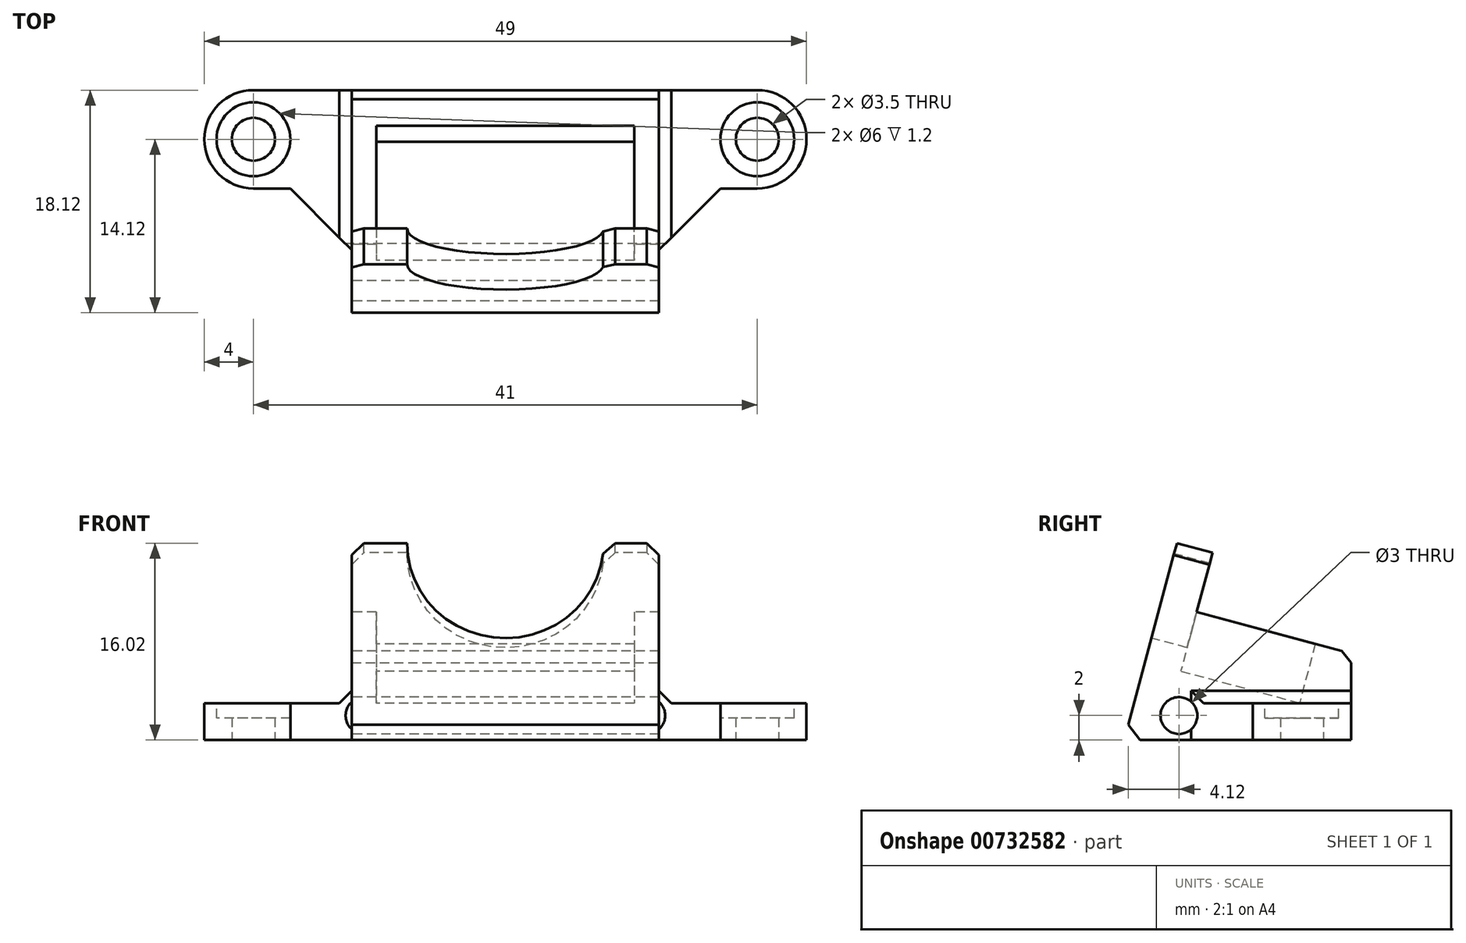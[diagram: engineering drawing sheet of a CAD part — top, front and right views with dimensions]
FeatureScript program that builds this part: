
annotation { "Feature Type Name" : "Feature", "Feature Type Description" : "" }
export const myFeature = defineFeature(function(context is Context, id is Id, definition is map)
    precondition{}
    {
        {
            var Q0;
            Q0=qCreatedBy(makeId("Top.planeOp"),FACE);
            var sketch = newSketch(context, id + "F0", { "sketchPlane" : qUnion([Q0])});
            skLineSegment(sketch, "E0.bottom", {"start": v(20.5, 4) * mm, "end": v(-20.5, 4) * mm});
            skLineSegment(sketch, "E0.top", {"start": v(20.5, -4) * mm, "end": v(-20.5, -4) * mm});
            skLineSegment(sketch, "E0.left", {"start": v(20.5, 4) * mm, "end": v(20.5, -4) * mm});
            skLineSegment(sketch, "E0.right", {"start": v(-20.5, 4) * mm, "end": v(-20.5, -4) * mm});
            skPoint(sketch, "E0.middle", {"position": v(0, 0) * mm});
            skCircle(sketch, "E1", {"center": v(20.5, 0) * mm, "radius": 4 * mm});
            skCircle(sketch, "E2", {"center": v(-20.5, 0) * mm, "radius": 4 * mm});
            skCircle(sketch, "E3", {"center": v(-20.5, 0) * mm, "radius": 1.75 * mm});
            skCircle(sketch, "E4", {"center": v(20.5, 0) * mm, "radius": 1.75 * mm});
            skSolve(sketch);
        }
        {
            var Q0;
            Q0=qCreatedBy(makeId("Right.planeOp"),FACE);
            var sketch = newSketch(context, id + "F1", { "sketchPlane" : qUnion([Q0])});
            skLineSegment(sketch, "E5", {"start": v(0, 0) * mm, "end": v(-14.45, 0) * mm});
            skLineSegment(sketch, "E6", {"start": v(-14.45, 0) * mm, "end": v(-10.16, 16.02) * mm});
            skLineSegment(sketch, "E7", {"start": v(-10.16, 16.02) * mm, "end": v(-7.26, 15.25) * mm});
            skLineSegment(sketch, "E8", {"start": v(-7.26, 15.25) * mm, "end": v(-9.85, 5.59) * mm});
            skLineSegment(sketch, "E9", {"start": v(-9.85, 5.59) * mm, "end": v(-0.2, 3) * mm});
            skLineSegment(sketch, "E10", {"start": v(-0.2, 3) * mm, "end": v(1.1, 7.83) * mm});
            skLineSegment(sketch, "E11", {"start": v(1.1, 7.83) * mm, "end": v(4, 7.05) * mm});
            skLineSegment(sketch, "E12", {"start": v(4, 0) * mm, "end": v(0, 0) * mm});
            skLineSegment(sketch, "E13", {"start": v(4, 7.05) * mm, "end": v(4, 0) * mm});
            skSolve(sketch);
        }
        {
            var Q0;
            Q0 = qSketchRegion(id + "F0", true);
            extrude(context, id + "F2", {"entities" : qUnion([Q0]), "depth" : 3 * mm, "offsetDistance" : 25 * mm});
        }
        {
            var Q0;
            Q0=makeQuery(id+"F2.opExtrude","CAP_FACE",FACE,{"disambiguationData":[OSD([sQuery(id+"F0.wireOp",EDGE,"E0.bottom"),sQuery(id+"F0.wireOp",EDGE,"E0.top"),sQuery(id+"F0.wireOp",EDGE,"E1"),sQuery(id+"F0.wireOp",EDGE,"E2"),sQuery(id+"F0.wireOp",EDGE,"E3"),sQuery(id+"F0.wireOp",EDGE,"E4")])],"isStart":false});
            var sketch = newSketch(context, id + "F3", { "sketchPlane" : qUnion([Q0])});
            skCircle(sketch, "E14", {"center": v(-20.5, 0) * mm, "radius": 3 * mm});
            skCircle(sketch, "E15", {"center": v(20.5, 0) * mm, "radius": 3 * mm});
            skSolve(sketch);
        }
        {
            var Q0;
            Q0 = qSketchRegion(id + "F3", true);
            extrude(context, id + "F4", {"entities" : qUnion([Q0]), "operationType" : NewBodyOperationType.REMOVE, "oppositeDirection" : true, "depth" : 1.2 * mm, "offsetDistance" : 25 * mm});
        }
        {
            var Q0;
            Q0 = qSketchRegion(id + "F1", true);
            extrude(context, id + "F5", {"entities" : qUnion([Q0]), "operationType" : NewBodyOperationType.ADD, "endBound" : BoundingType.SYMMETRIC, "depth" : 25 * mm, "offsetDistance" : 25 * mm});
        }
        {
            var Q0;
            Q0=makeQuery(id+"F5.opExtrude","SWEPT_FACE",FACE,{"disambiguationData":[OSD([sQuery(id+"F1.wireOp",EDGE,"E9")])]});
            var sketch = newSketch(context, id + "F6", { "sketchPlane" : qUnion([Q0])});
            skLineSegment(sketch, "E16", {"start": v(10.5, -10.96) * mm, "end": v(10.5, -0.96) * mm});
            skLineSegment(sketch, "E17", {"start": v(10.5, -0.96) * mm, "end": v(-10.5, -0.96) * mm, "construction": true});
            skLineSegment(sketch, "E18", {"start": v(-10.5, -0.96) * mm, "end": v(-10.5, -10.96) * mm});
            skLineSegment(sketch, "E19", {"start": v(-10.5, -10.96) * mm, "end": v(10.5, -10.96) * mm, "construction": true});
            skPoint(sketch, "E20", {"position": v(0, -0.96) * mm});
            skLineSegment(sketch, "E21", {"start": v(0, 0) * mm, "end": v(0, -0.96) * mm, "construction": true});
            skLineSegment(sketch, "E22.0", {"start": v(12.5, -10.96) * mm, "end": v(12.5, -0.96) * mm});
            skLineSegment(sketch, "E23.0", {"start": v(-12.5, -10.96) * mm, "end": v(-12.5, -0.96) * mm});
            skLineSegment(sketch, "E24", {"start": v(-10.5, -10.96) * mm, "end": v(-12.5, -10.96) * mm});
            skLineSegment(sketch, "E25", {"start": v(-10.5, -0.96) * mm, "end": v(-12.5, -0.96) * mm});
            skLineSegment(sketch, "E26", {"start": v(10.5, -0.96) * mm, "end": v(12.5, -0.96) * mm});
            skLineSegment(sketch, "E27", {"start": v(12.5, -10.96) * mm, "end": v(10.5, -10.96) * mm});
            skSolve(sketch);
        }
        {
            var Q0;
            Q0 = qSketchRegion(id + "F6", true);
            var Q1;
            Q1=makeQuery(id+"F5.opExtrude","SWEPT_FACE",FACE,{"disambiguationData":[OSD([sQuery(id+"F1.wireOp",EDGE,"E11")])]});
            extrude(context, id + "F7", {"entities" : qUnion([Q0]), "operationType" : NewBodyOperationType.ADD, "endBound" : BoundingType.UP_TO_SURFACE, "depth" : 25 * mm, "endBoundEntityFace" : qUnion([Q1]), "offsetDistance" : 25 * mm});
        }
        {
            var Q0;
            Q0=makeQuery(id+"F5.opExtrude","SWEPT_FACE",FACE,{"disambiguationData":[OSD([sQuery(id+"F1.wireOp",EDGE,"E6")])]});
            var sketch = newSketch(context, id + "F8", { "sketchPlane" : qUnion([Q0])});
            skCircle(sketch, "E28", {"center": v(0, 12.85) * mm, "radius": 8 * mm});
            skSolve(sketch);
        }
        {
            var Q0;
            {var subQ0=sQuery(id+"F8.wireOp",EDGE,"E28");var subQ1=makeQuery(id+"F5.opExtrude","SWEPT_EDGE",EDGE,{"disambiguationData":[OSD([sQuery(id+"F1.wireOp",EDGE,"E6"),sQuery(id+"F1.wireOp",EDGE,"E7")])]});var subQ2=makeQuery(id+"F8.imprint","INTERSECT",VERTEX,{"disambiguationData":[OD(0.0)],"derivedFrom":[subQ1,subQ0]});Q0=makeQuery(id+"F8.imprint","IMPRINT",FACE,{"disambiguationData":[TD([[makeQuery(id+"F8.imprint","IMPRINT",EDGE,{"disambiguationData":[TD([[subQ2,-1.0]])],"derivedFrom":subQ0}),1.0]])]});}
            extrude(context, id + "F9", {"entities" : qUnion([Q0]), "operationType" : NewBodyOperationType.REMOVE, "endBound" : BoundingType.UP_TO_NEXT, "oppositeDirection" : true, "depth" : 25 * mm, "offsetDistance" : 25 * mm});
        }
        {
            var Q0;
            Q0=makeQuery(id+"F5.boolean.opBoolean","INTERSECT",EDGE,{"derivedFrom":[makeQuery(id+"F2.opExtrude","SWEPT_FACE",FACE,{"disambiguationData":[OSD([sQuery(id+"F0.wireOp",EDGE,"E0.top")])]}),makeQuery(id+"F5.opExtrude","CAP_FACE",FACE,{"disambiguationData":[OSD([sQuery(id+"F1.wireOp",EDGE,"E5"),sQuery(id+"F1.wireOp",EDGE,"E6"),sQuery(id+"F1.wireOp",EDGE,"E7"),sQuery(id+"F1.wireOp",EDGE,"E8"),sQuery(id+"F1.wireOp",EDGE,"E9"),sQuery(id+"F1.wireOp",EDGE,"E10"),sQuery(id+"F1.wireOp",EDGE,"E11"),sQuery(id+"F1.wireOp",EDGE,"E12"),sQuery(id+"F1.wireOp",EDGE,"E13")])],"isStart":true})]});
            var Q1;
            Q1=makeQuery(id+"F5.boolean.opBoolean","INTERSECT",EDGE,{"derivedFrom":[makeQuery(id+"F2.opExtrude","SWEPT_FACE",FACE,{"disambiguationData":[OSD([sQuery(id+"F0.wireOp",EDGE,"E0.top")])]}),makeQuery(id+"F5.opExtrude","CAP_FACE",FACE,{"disambiguationData":[OSD([sQuery(id+"F1.wireOp",EDGE,"E5"),sQuery(id+"F1.wireOp",EDGE,"E6"),sQuery(id+"F1.wireOp",EDGE,"E7"),sQuery(id+"F1.wireOp",EDGE,"E8"),sQuery(id+"F1.wireOp",EDGE,"E9"),sQuery(id+"F1.wireOp",EDGE,"E10"),sQuery(id+"F1.wireOp",EDGE,"E11"),sQuery(id+"F1.wireOp",EDGE,"E12"),sQuery(id+"F1.wireOp",EDGE,"E13")])],"isStart":false})]});
            chamfer(context, id + "F10", {"entities" : qUnion([Q0, Q1]), "width" : 5 * mm, "tangentPropagation" : true});
        }
        {
            var Q0;
            {var subQ0=sQuery(id+"F8.wireOp",EDGE,"E28");var subQ1=sQuery(id+"F1.wireOp",EDGE,"E7");var subQ2=sQuery(id+"F1.wireOp",EDGE,"E6");Q0=makeQuery(id+"F9.boolean.opBoolean","COPY",EDGE,{"derivedFrom":makeQuery(id+"F9.opExtrude","SWEPT_EDGE",EDGE,{"disambiguationData":[OSD([subQ2,subQ1,subQ0]),TDD([makeQuery(id+"F8.imprint","INTERSECT",VERTEX,{"disambiguationData":[OD(0.0)],"derivedFrom":[makeQuery(id+"F5.opExtrude","SWEPT_EDGE",EDGE,{"disambiguationData":[OSD([subQ2,subQ1])]}),subQ0]})])]})});}
            var Q1;
            {var subQ0=sQuery(id+"F8.wireOp",EDGE,"E28");var subQ1=sQuery(id+"F1.wireOp",EDGE,"E7");var subQ2=sQuery(id+"F1.wireOp",EDGE,"E6");Q1=makeQuery(id+"F9.boolean.opBoolean","COPY",EDGE,{"derivedFrom":makeQuery(id+"F9.opExtrude","SWEPT_EDGE",EDGE,{"disambiguationData":[OSD([subQ2,subQ1,subQ0]),TDD([makeQuery(id+"F8.imprint","INTERSECT",VERTEX,{"disambiguationData":[OD(1.0)],"derivedFrom":[makeQuery(id+"F5.opExtrude","SWEPT_EDGE",EDGE,{"disambiguationData":[OSD([subQ2,subQ1])]}),subQ0]})])]})});}
            var Q2;
            Q2=makeQuery(id+"F7.opExtrude","CAP_EDGE",EDGE,{"disambiguationData":[OSD([sQuery(id+"F6.wireOp",EDGE,"E18")])],"isStart":true});
            var Q3;
            Q3=makeQuery(id+"F7.opExtrude","CAP_EDGE",EDGE,{"disambiguationData":[OSD([sQuery(id+"F6.wireOp",EDGE,"E16")])],"isStart":true});
            var Q4;
            {var subQ0=makeQuery(id+"F5.opExtrude","CAP_FACE",FACE,{"disambiguationData":[OSD([sQuery(id+"F1.wireOp",EDGE,"E5"),sQuery(id+"F1.wireOp",EDGE,"E6"),sQuery(id+"F1.wireOp",EDGE,"E7"),sQuery(id+"F1.wireOp",EDGE,"E8"),sQuery(id+"F1.wireOp",EDGE,"E9"),sQuery(id+"F1.wireOp",EDGE,"E10"),sQuery(id+"F1.wireOp",EDGE,"E11"),sQuery(id+"F1.wireOp",EDGE,"E12"),sQuery(id+"F1.wireOp",EDGE,"E13")])],"isStart":false});var subQ1=makeQuery(id+"F2.opExtrude","CAP_FACE",FACE,{"disambiguationData":[OSD([sQuery(id+"F0.wireOp",EDGE,"E0.bottom"),sQuery(id+"F0.wireOp",EDGE,"E0.top"),sQuery(id+"F0.wireOp",EDGE,"E1"),sQuery(id+"F0.wireOp",EDGE,"E2"),sQuery(id+"F0.wireOp",EDGE,"E3"),sQuery(id+"F0.wireOp",EDGE,"E4")])],"isStart":false});Q4=makeQuery(id+"F7.boolean.opBoolean","MERGE",EDGE,{"derivedFrom":[makeQuery(id+"F5.boolean.opBoolean","INTERSECT",EDGE,{"disambiguationData":[OD(0.0)],"derivedFrom":[subQ1,subQ0]}),makeQuery(id+"F5.boolean.opBoolean","INTERSECT",EDGE,{"disambiguationData":[OD(1.0)],"derivedFrom":[subQ1,subQ0]})]});}
            var Q5;
            {var subQ0=makeQuery(id+"F5.opExtrude","CAP_FACE",FACE,{"disambiguationData":[OSD([sQuery(id+"F1.wireOp",EDGE,"E5"),sQuery(id+"F1.wireOp",EDGE,"E6"),sQuery(id+"F1.wireOp",EDGE,"E7"),sQuery(id+"F1.wireOp",EDGE,"E8"),sQuery(id+"F1.wireOp",EDGE,"E9"),sQuery(id+"F1.wireOp",EDGE,"E10"),sQuery(id+"F1.wireOp",EDGE,"E11"),sQuery(id+"F1.wireOp",EDGE,"E12"),sQuery(id+"F1.wireOp",EDGE,"E13")])],"isStart":true});var subQ1=makeQuery(id+"F2.opExtrude","CAP_FACE",FACE,{"disambiguationData":[OSD([sQuery(id+"F0.wireOp",EDGE,"E0.bottom"),sQuery(id+"F0.wireOp",EDGE,"E0.top"),sQuery(id+"F0.wireOp",EDGE,"E1"),sQuery(id+"F0.wireOp",EDGE,"E2"),sQuery(id+"F0.wireOp",EDGE,"E3"),sQuery(id+"F0.wireOp",EDGE,"E4")])],"isStart":false});Q5=makeQuery(id+"F7.boolean.opBoolean","MERGE",EDGE,{"derivedFrom":[makeQuery(id+"F5.boolean.opBoolean","INTERSECT",EDGE,{"disambiguationData":[OD(0.0)],"derivedFrom":[subQ1,subQ0]}),makeQuery(id+"F5.boolean.opBoolean","INTERSECT",EDGE,{"disambiguationData":[OD(1.0)],"derivedFrom":[subQ1,subQ0]})]});}
            var Q6;
            Q6=makeQuery(id+"F5.opExtrude","SWEPT_EDGE",EDGE,{"disambiguationData":[OSD([sQuery(id+"F1.wireOp",EDGE,"E5"),sQuery(id+"F1.wireOp",EDGE,"E6")])]});
            var Q7;
            Q7=makeQuery(id+"F5.opExtrude","CAP_EDGE",EDGE,{"disambiguationData":[OSD([sQuery(id+"F1.wireOp",EDGE,"E7")])],"isStart":true});
            var Q8;
            Q8=makeQuery(id+"F5.opExtrude","CAP_EDGE",EDGE,{"disambiguationData":[OSD([sQuery(id+"F1.wireOp",EDGE,"E7")])],"isStart":false});
            var Q9;
            Q9=makeQuery(id+"F5.opExtrude","SWEPT_EDGE",EDGE,{"disambiguationData":[OSD([sQuery(id+"F1.wireOp",EDGE,"E11"),sQuery(id+"F1.wireOp",EDGE,"E13")])]});
            chamfer(context, id + "F11", {"entities" : qUnion([Q0, Q1, Q2, Q3, Q4, Q5, Q6, Q7, Q8, Q9]), "width" : 1 * mm, "tangentPropagation" : true});
        }
        {
            var Q0;
            {var subQ0=sQuery(id+"F0.wireOp",EDGE,"E0.top");var subQ5=sQuery(id+"F0.wireOp",EDGE,"E0.bottom");var subQ7=sQuery(id+"F1.wireOp",EDGE,"E13");var subQ8=sQuery(id+"F1.wireOp",EDGE,"E12");var subQ9=sQuery(id+"F1.wireOp",EDGE,"E11");var subQ10=sQuery(id+"F1.wireOp",EDGE,"E10");var subQ11=sQuery(id+"F1.wireOp",EDGE,"E9");var subQ12=sQuery(id+"F1.wireOp",EDGE,"E8");var subQ13=sQuery(id+"F1.wireOp",EDGE,"E7");var subQ14=sQuery(id+"F1.wireOp",EDGE,"E6");var subQ15=sQuery(id+"F1.wireOp",EDGE,"E5");var subQ16=makeQuery(id+"F5.opExtrude","CAP_FACE",FACE,{"disambiguationData":[OSD([subQ15,subQ14,subQ13,subQ12,subQ11,subQ10,subQ9,subQ8,subQ7])],"isStart":true});Q0=makeQuery(id+"F7.boolean.opBoolean","MERGE",FACE,{"derivedFrom":[makeQuery(id+"F5.boolean.opBoolean","SPLIT",FACE,{"disambiguationData":[TD([makeQuery(id+"F2.opExtrude","SWEPT_FACE",FACE,{"disambiguationData":[OSD([subQ5])]})])],"derivedFrom":subQ16}),makeQuery(id+"F5.boolean.opBoolean","SPLIT",FACE,{"disambiguationData":[TD([makeQuery(id+"F2.opExtrude","SWEPT_FACE",FACE,{"disambiguationData":[OSD([subQ0])]})])],"derivedFrom":subQ16}),makeQuery(id+"F7.opExtrude","SWEPT_FACE",FACE,{"disambiguationData":[OSD([sQuery(id+"F6.wireOp",EDGE,"E23.0")])]})]});}
            var sketch = newSketch(context, id + "F12", { "sketchPlane" : qUnion([Q0])});
            skCircle(sketch, "E29", {"center": v(10, 2) * mm, "radius": 1.5 * mm});
            skSolve(sketch);
        }
        {
            var Q0;
            Q0 = qSketchRegion(id + "F12", true);
            extrude(context, id + "F13", {"entities" : qUnion([Q0]), "operationType" : NewBodyOperationType.REMOVE, "endBound" : BoundingType.THROUGH_ALL, "oppositeDirection" : true, "depth" : 25 * mm, "offsetDistance" : 25 * mm, "hasSecondDirection" : true, "secondDirectionBound" : SecondDirectionBoundingType.THROUGH_ALL, "secondDirectionOppositeDirection" : false, "secondDirectionDepth" : 25 * mm});
        }
    });
